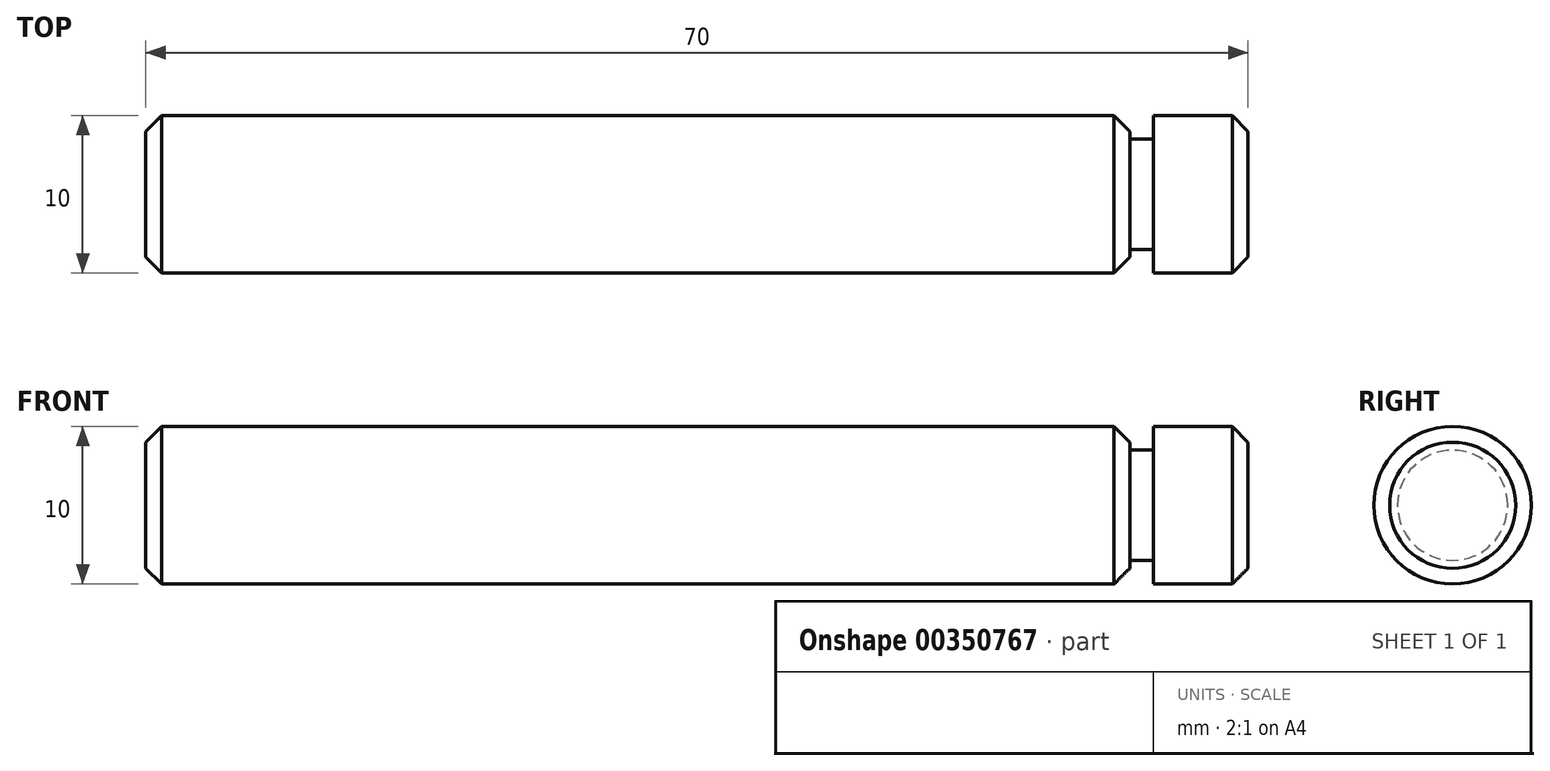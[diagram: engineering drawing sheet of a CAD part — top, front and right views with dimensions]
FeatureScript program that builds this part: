
annotation { "Feature Type Name" : "Feature", "Feature Type Description" : "" }
export const myFeature = defineFeature(function(context is Context, id is Id, definition is map)
    precondition{}
    {
        {
            var Q0;
            Q0=qCreatedBy(makeId("Front.planeOp"),FACE);
            var sketch = newSketch(context, id + "F0", { "sketchPlane" : qUnion([Q0])});
            skLineSegment(sketch, "E0", {"start": v(-83.15, 0) * mm, "end": v(-13.15, 0) * mm});
            skLineSegment(sketch, "E1.0", {"start": v(-83.15, 5) * mm, "end": v(-20.65, 5) * mm});
            skLineSegment(sketch, "E2", {"start": v(-13.15, 5) * mm, "end": v(-13.15, 0) * mm});
            skLineSegment(sketch, "E3.0", {"start": v(-19.15, 5) * mm, "end": v(-19.15, 3.5) * mm});
            skLineSegment(sketch, "E4", {"start": v(-83.15, 0) * mm, "end": v(-83.15, 5) * mm});
            skLineSegment(sketch, "E5.0", {"start": v(-20.65, 5) * mm, "end": v(-20.65, 3.5) * mm});
            skLineSegment(sketch, "E6.trimOffspring", {"start": v(-20.65, 3.5) * mm, "end": v(-19.15, 3.5) * mm});
            skLineSegment(sketch, "E7.trimOffspring", {"start": v(-19.15, 5) * mm, "end": v(-13.15, 5) * mm});
            skLineSegment(sketch, "E8.bottom", {"start": v(-74.93, 0) * mm, "end": v(-112.8, 0) * mm});
            skLineSegment(sketch, "E8.top", {"start": v(-74.93, 5) * mm, "end": v(-114.93, 5) * mm});
            skLineSegment(sketch, "E9.top", {"start": v(-74.93, -1) * mm, "end": v(-114.93, -1) * mm});
            skLineSegment(sketch, "E9.left", {"start": v(-74.93, 0) * mm, "end": v(-74.93, -1) * mm});
            skLineSegment(sketch, "E9.right", {"start": v(-114.93, 0) * mm, "end": v(-114.93, -1) * mm});
            skLineSegment(sketch, "E10", {"start": v(-114.93, 0) * mm, "end": v(-114.93, 5) * mm});
            skLineSegment(sketch, "E11", {"start": v(-112.8, -1) * mm, "end": v(-112.8, 5) * mm});
            skSolve(sketch);
        }
        {
            var Q0;
            {var subQ1=sQuery(id+"F0.wireOp",EDGE,"E0");Q0=makeQuery(id+"F0.imprint","IMPRINT",FACE,{"disambiguationData":[TD([[makeQuery(id+"F0.imprint","IMPRINT",EDGE,{"derivedFrom":subQ1}),1.0]])]});}
            var Q1;
            Q1=sQuery(id+"F0.wireOp",EDGE,"E0");
            revolve(context, id + "F1", {"entities" : qUnion([Q0]), "axis" : qUnion([Q1]), "revolveType" : RevolveType.FULL});
        }
        {
            var Q0;
            Q0=makeQuery(id+"F1.opRevolve","SWEPT_EDGE",EDGE,{"disambiguationData":[OSD([sQuery(id+"F0.wireOp",EDGE,"a03fbee8-2e0a-4c8b-9d5f-491997530557.0"),sQuery(id+"F0.wireOp",EDGE,"E4")])]});
            var Q1;
            Q1=makeQuery(id+"F1.opRevolve","SWEPT_EDGE",EDGE,{"disambiguationData":[OSD([sQuery(id+"F0.wireOp",EDGE,"E1.0"),sQuery(id+"F0.wireOp",EDGE,"828546c2-3b29-4b0d-96e1-b25bbb1505cc.0")])]});
            var Q2;
            Q2=makeQuery(id+"F1.opRevolve","SWEPT_EDGE",EDGE,{"disambiguationData":[OSD([sQuery(id+"F0.wireOp",EDGE,"E2"),sQuery(id+"F0.wireOp",EDGE,"E7.trimOffspring")])]});
            var Q3;
            Q3=makeQuery(id+"F1.opRevolve","SWEPT_EDGE",EDGE,{"disambiguationData":[OSD([sQuery(id+"F0.wireOp",EDGE,"E1.0"),sQuery(id+"F0.wireOp",EDGE,"E5.0")])]});
            chamfer(context, id + "F2", {"entities" : qUnion([Q0, Q1, Q2, Q3]), "width" : 1 * mm, "tangentPropagation" : true});
        }
    });
